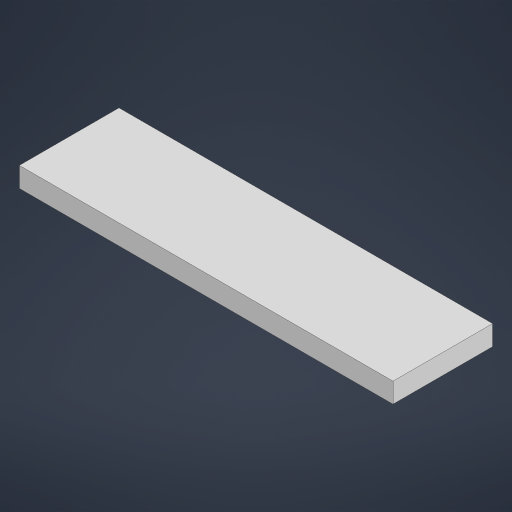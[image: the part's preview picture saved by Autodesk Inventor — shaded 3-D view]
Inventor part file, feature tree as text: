
AUTODESK INVENTOR PART (.ipt)
format: ipt  version: 2024.3 (Build 283343000, 343)  size: 169,984 bytes
history: native  units: mm
features: extrude x1, sketch x1
ambient origin geometry x8: Origin, YZ Plane, XZ Plane, XY Plane, X Axis, Y Axis, Z Axis, Center Point
bodies: Solid1 (feature_tree)
feature tree (2):
  extrude  "Extrusion1"  Depth=40.0mm
  sketch  "Sketch1"  dims[d0=150.0mm d1=40.0mm d2=8.0mm d3=0.0mm]
